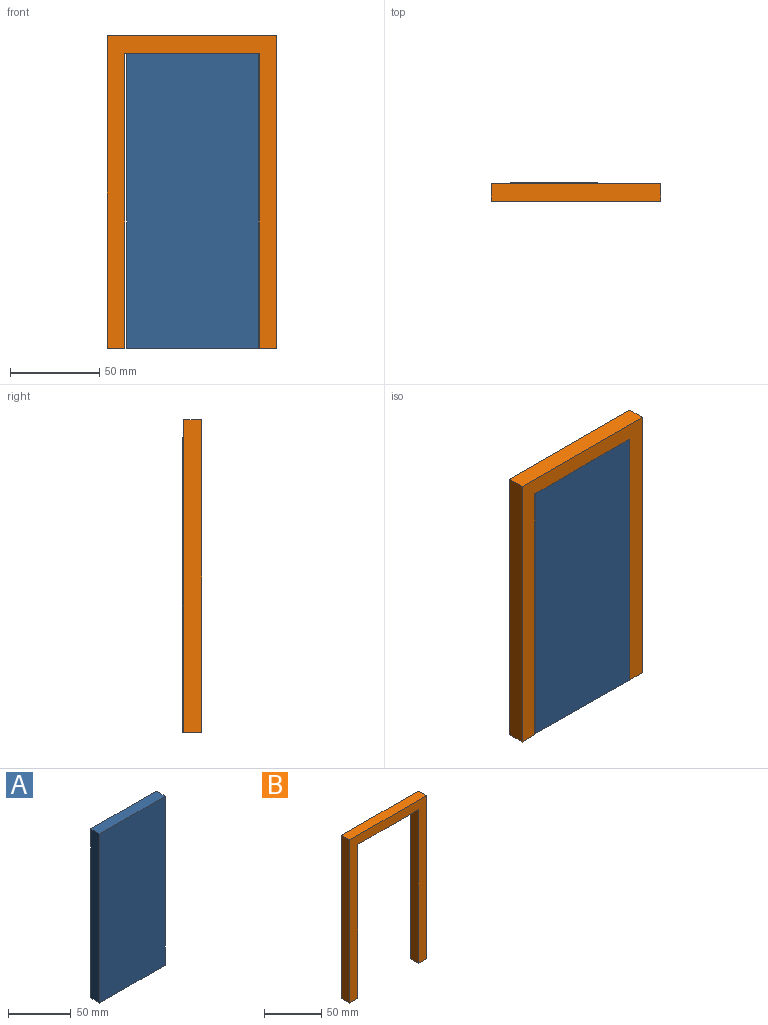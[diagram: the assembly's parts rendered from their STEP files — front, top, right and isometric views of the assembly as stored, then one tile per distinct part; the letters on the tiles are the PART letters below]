
ASSEMBLY  parts=2 mates=1
PART A: 6 faces, bbox 74x10x165 mm
  f0: plane 165x10mm, normal (-1,0,0), area 1650mm2, adj f1,f3,f4,f5
  f1: plane 74x10mm, normal (0,0,-1), area 740mm2, adj f0,f2,f4,f5
  f2: plane 165x10mm, normal (1,0,0), area 1650mm2, adj f1,f3,f4,f5
  f3: plane 74x10mm, normal (0,0,1), area 740mm2, adj f0,f2,f4,f5
  f4: plane 165x74mm, normal (0,-1,0), area 12210mm2, adj f0,f1,f2,f3
  f5: plane 165x74mm, normal (0,1,0), area 12210mm2, adj f0,f1,f2,f3
PART B: 10 faces, bbox 95x10x175 mm
  f0: plane 165x10mm, normal (-1,0,0), area 1650mm2, adj f1,f7,f8,f9
  f1: plane 10x10mm, normal (0,0,-1), area 100mm2, adj f0,f2,f8,f9
  f2: plane 175x10mm, normal (1,0,0), area 1750mm2, adj f1,f3,f8,f9
  f3: plane 95x10mm, normal (0,0,1), area 950mm2, adj f2,f4,f8,f9
  f4: plane 175x10mm, normal (-1,0,0), area 1750mm2, adj f3,f5,f8,f9
  f5: plane 10x10mm, normal (0,0,-1), area 100mm2, adj f4,f6,f8,f9
  f6: plane 165x10mm, normal (1,0,0), area 1650mm2, adj f5,f7,f8,f9
  f7: plane 75x10mm, normal (0,0,-1), area 750mm2, adj f0,f6,f8,f9
  f8: plane 175x95mm, normal (0,-1,0), area 4250mm2, adj f0,f1,f2,f3,f4,f5,f6,f7
  f9: plane 175x95mm, normal (0,1,0), area 4250mm2, adj f0,f1,f2,f3,f4,f5,f6,f7
PLACE A rot(axis=(0,0,-1),0.5deg) t=(-27.38,83.12,-45.61)mm
PLACE B t=(80.88,83.22,54.78)mm fixed
MATE revolute A.f1 <-> B.f1  axis (0,0,-1) through (-38.38,83.22,-73.49)mm
